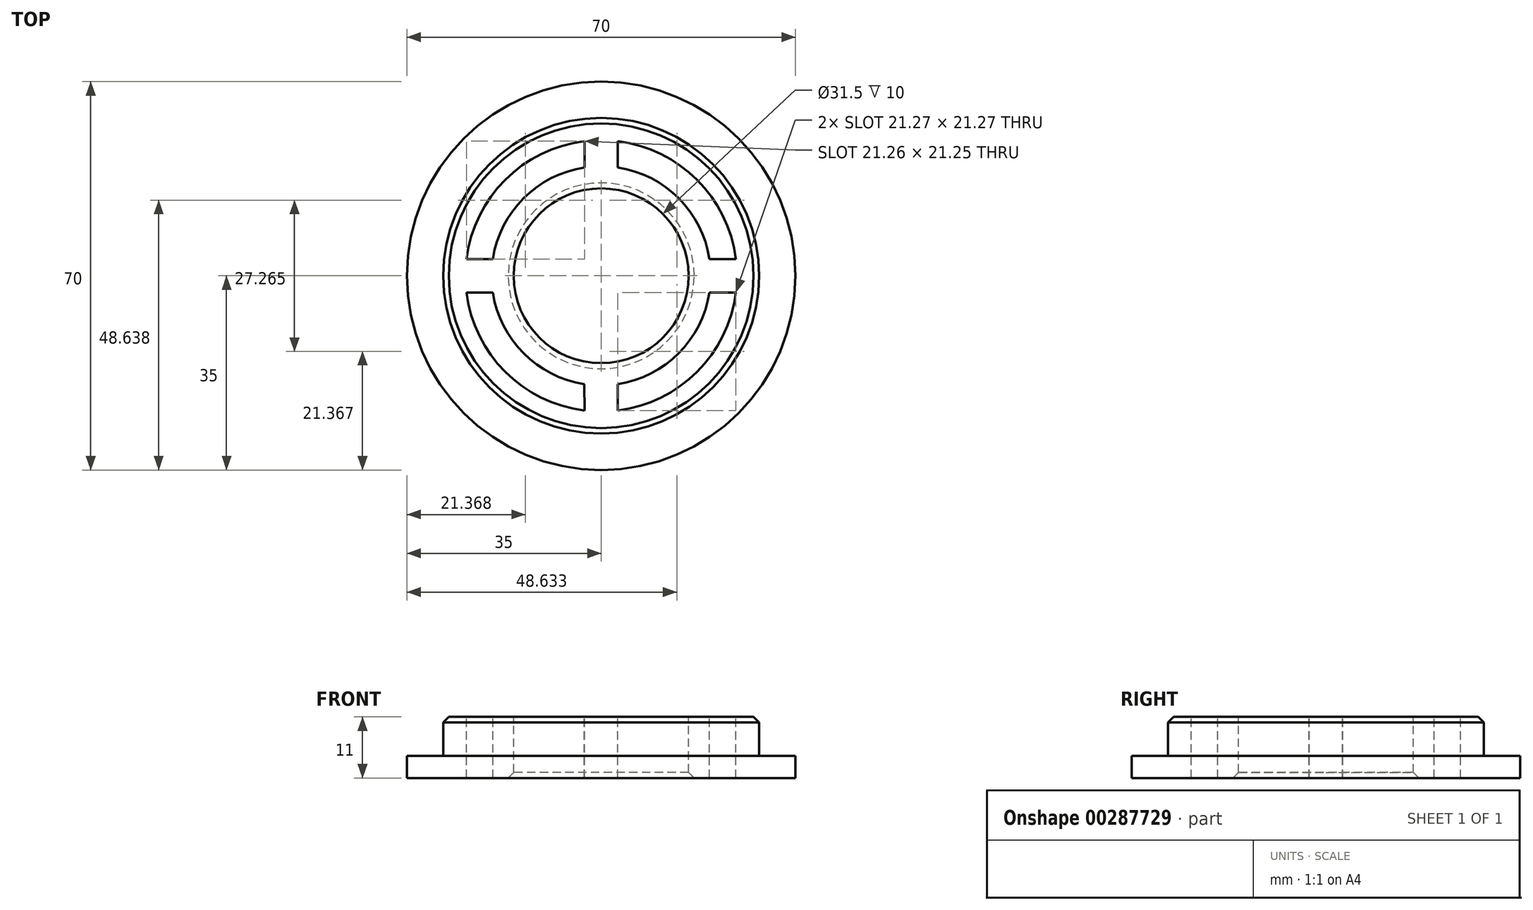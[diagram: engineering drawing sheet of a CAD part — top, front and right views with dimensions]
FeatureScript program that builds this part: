
annotation { "Feature Type Name" : "Feature", "Feature Type Description" : "" }
export const myFeature = defineFeature(function(context is Context, id is Id, definition is map)
    precondition{}
    {
        {
            var Q0;
            Q0=qCreatedBy(makeId("Top.planeOp"),FACE);
            var sketch = newSketch(context, id + "F0", { "sketchPlane" : qUnion([Q0])});
            skCircle(sketch, "E0", {"center": v(0, 0) * mm, "radius": 35 * mm});
            skSolve(sketch);
        }
        {
            var Q0;
            Q0 = qSketchRegion(id + "F0", true);
            extrude(context, id + "F1", {"entities" : qUnion([Q0]), "depth" : 4 * mm});
        }
        {
            var Q0;
            Q0=makeQuery(id+"F1.opExtrude","CAP_FACE",FACE,{"disambiguationData":[OSD([sQuery(id+"F0.wireOp",EDGE,"E0")])],"isStart":false});
            var sketch = newSketch(context, id + "F2", { "sketchPlane" : qUnion([Q0])});
            skCircle(sketch, "E1", {"center": v(0, 0) * mm, "radius": 28.45 * mm});
            skSolve(sketch);
        }
        {
            var Q0;
            Q0 = qSketchRegion(id + "F2", true);
            extrude(context, id + "F3", {"entities" : qUnion([Q0]), "operationType" : NewBodyOperationType.ADD, "depth" : 7 * mm});
        }
        {
            var Q0;
            Q0=makeQuery(id+"F3.opExtrude","CAP_FACE",FACE,{"disambiguationData":[OSD([sQuery(id+"F2.wireOp",EDGE,"E1")])],"isStart":false});
            var sketch = newSketch(context, id + "F4", { "sketchPlane" : qUnion([Q0])});
            skArc(sketch, "E2.0", {"start": v(24.27, 3) * mm, "mid": v(17.29, 17.29) * mm, "end": v(3, 24.27) * mm});
            skArc(sketch, "E3.0", {"start": v(19.52, 3) * mm, "mid": v(13.97, 13.97) * mm, "end": v(3, 19.52) * mm});
            skLineSegment(sketch, "E4.bottom", {"start": v(24.27, -3) * mm, "end": v(19.52, -3) * mm});
            skLineSegment(sketch, "E4.top", {"start": v(24.27, 3) * mm, "end": v(19.52, 3) * mm});
            skLineSegment(sketch, "E5.left", {"start": v(3, 24.27) * mm, "end": v(3, 19.52) * mm});
            skLineSegment(sketch, "E5.right", {"start": v(-3, 24.27) * mm, "end": v(-3, 19.52) * mm});
            skPoint(sketch, "E6.orphan", {"position": v(26, 3) * mm});
            skPoint(sketch, "E7.orphan", {"position": v(26, -3) * mm});
            skArc(sketch, "E8.trimOffspring", {"start": v(-3, 19.52) * mm, "mid": v(-13.95, 13.98) * mm, "end": v(-19.51, 3.04) * mm});
            skArc(sketch, "E9.trimOffspring", {"start": v(-3, 24.27) * mm, "mid": v(-17.29, 17.3) * mm, "end": v(-24.26, 3.01) * mm});
            skLineSegment(sketch, "E10.trimOffspring", {"start": v(3, -19.52) * mm, "end": v(3, -24.27) * mm});
            skPoint(sketch, "E11.orphan", {"position": v(3, 25.82) * mm});
            skPoint(sketch, "E12.orphan", {"position": v(-3, 25.82) * mm});
            skLineSegment(sketch, "E13.trimOffspring", {"start": v(-19.51, 3.04) * mm, "end": v(-24.26, 3.01) * mm});
            skLineSegment(sketch, "E14.trimOffspring", {"start": v(-19.51, -3.04) * mm, "end": v(-24.26, -3.01) * mm});
            skLineSegment(sketch, "E15.trimOffspring", {"start": v(-3.04, -19.51) * mm, "end": v(-3, -24.26) * mm});
            skPoint(sketch, "E16.orphan", {"position": v(3, -25.82) * mm});
            skPoint(sketch, "E17.orphan", {"position": v(-3, -25.82) * mm});
            skArc(sketch, "E18.trimOffspring", {"start": v(3, -19.52) * mm, "mid": v(13.97, -13.97) * mm, "end": v(19.52, -3) * mm});
            skArc(sketch, "E19.trimOffspring", {"start": v(3, -24.27) * mm, "mid": v(17.29, -17.29) * mm, "end": v(24.27, -3) * mm});
            skPoint(sketch, "E20.orphan", {"position": v(-26, 3) * mm});
            skPoint(sketch, "E21.orphan", {"position": v(-26, -3) * mm});
            skArc(sketch, "E22.trimOffspring", {"start": v(-19.51, -3.04) * mm, "mid": v(-13.97, -13.97) * mm, "end": v(-3.04, -19.51) * mm});
            skArc(sketch, "E23.trimOffspring", {"start": v(-24.26, -3.01) * mm, "mid": v(-17.29, -17.29) * mm, "end": v(-3, -24.26) * mm});
            skCircle(sketch, "E24.converted", {"center": v(0, 0) * mm, "radius": 15.75 * mm});
            skSolve(sketch);
        }
        {
            var Q0;
            Q0 = qSketchRegion(id + "F4", true);
            extrude(context, id + "F5", {"entities" : qUnion([Q0]), "operationType" : NewBodyOperationType.REMOVE, "endBound" : BoundingType.THROUGH_ALL, "oppositeDirection" : true, "depth" : 25 * mm});
        }
        {
            var Q0;
            Q0=makeQuery(id+"F3.opExtrude","CAP_EDGE",EDGE,{"disambiguationData":[OSD([sQuery(id+"F2.wireOp",EDGE,"E1")])],"isStart":false});
            var Q1;
            Q1=makeQuery(id+"F5.boolean.opBoolean","INTERSECT",EDGE,{"derivedFrom":[makeQuery(id+"F1.opExtrude","CAP_FACE",FACE,{"disambiguationData":[OSD([sQuery(id+"F0.wireOp",EDGE,"E0")])],"isStart":true}),makeQuery(id+"F5.opExtrude","SWEPT_FACE",FACE,{"disambiguationData":[OSD([sQuery(id+"F4.wireOp",EDGE,"E24.converted")])]})]});
            chamfer(context, id + "F6", {"entities" : qUnion([Q0, Q1]), "width" : 1 * mm, "tangentPropagation" : true});
        }
    });
